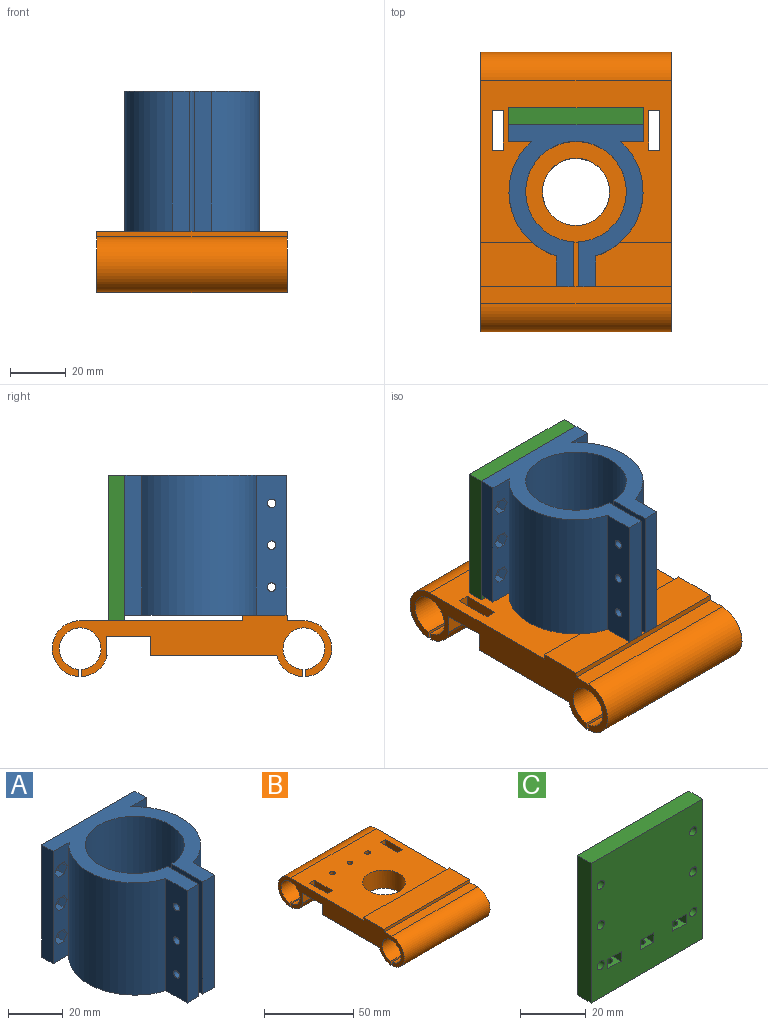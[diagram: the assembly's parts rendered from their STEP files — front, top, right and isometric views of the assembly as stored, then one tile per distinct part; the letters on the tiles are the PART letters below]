
ASSEMBLY  parts=3 mates=2
PART A: 91 faces, bbox 48x58x50 mm
  f0: cylinder r=24mm len=50mm, axis (0,0,-1), area 2547.5mm2, adj f1,f13,f14,f15
  f1: plane 50x8.13mm, normal (0,-1,0), area 331.4mm2, adj f0,f2,f14,f15,f43,f44,f45,f46
  f2: plane 50x6mm, normal (1,0,0), area 300mm2, adj f1,f3,f14,f15
  f3: plane 50x48mm, normal (0,1,0), area 2354.7mm2, adj f2,f4,f14,f15,f64,f65,f66,f88
  f4: plane 50x6mm, normal (-1,0,0), area 300mm2, adj f3,f5,f14,f15
  f5: plane 50x8.13mm, normal (0,-1,0), area 331.4mm2, adj f4,f6,f14,f15,f67,f68,f69,f70
  f6: cylinder r=24mm len=50mm, axis (0,0,-1), area 2547.5mm2, adj f5,f7,f14,f15
  f7: plane 50x11.02mm, normal (-1,0,0), area 528.5mm2, adj f6,f8,f14,f15,f40,f41,f42
  f8: plane 50x6mm, normal (0,-1,0), area 300mm2, adj f7,f9,f14,f15
  f9: plane 50x16.01mm, normal (1,0,0), area 777.7mm2, adj f8,f10,f14,f15,f40,f41,f42
  f10: cylinder r=18mm len=50mm, axis (0,0,-1), area 5554.8mm2, adj f9,f11,f14,f15
  f11: plane 50x16.01mm, normal (-1,0,0), area 777.7mm2, adj f10,f12,f14,f15,f37,f38,f39
  f12: plane 50x6mm, normal (0,-1,0), area 300mm2, adj f11,f13,f14,f15
  f13: plane 50x11.02mm, normal (1,0,0), area 476.2mm2, adj f0,f12,f14,f15,f16,f17,f18,f19
  f14: plane 57.98x48mm, normal (0,0,1), area 1061.7mm2, adj f0,f1,f2,f3,f4,f5,f6,f7
  f15: plane 57.98x48mm, normal (0,0,-1), area 1061.7mm2, adj f0,f1,f2,f3,f4,f5,f6,f7
  f16: plane 3.3x3.1mm, normal (0,0,1), area 10.2mm2, adj f13,f17,f21,f22
  f17: plane 3.3x2.68mm, normal (0,-0.87,0.5), area 10.2mm2, adj f13,f16,f18,f22
  f18: plane 3.3x2.68mm, normal (0,-0.87,-0.5), area 10.2mm2, adj f13,f17,f19,f22
  f19: plane 3.3x3.1mm, normal (0,0,-1), area 10.2mm2, adj f13,f18,f20,f22
  f20: plane 3.3x2.68mm, normal (0,0.87,-0.5), area 10.2mm2, adj f13,f19,f21,f22
  f21: plane 3.3x2.68mm, normal (0,0.87,0.5), area 10.2mm2, adj f13,f16,f20,f22
  f22: plane 6.2x5.37mm, normal (1,0,0), area 17.4mm2, adj f16,f17,f18,f19,f20,f21,f39
  f23: plane 3.3x3.1mm, normal (0,0,1), area 10.2mm2, adj f13,f24,f28,f29
  f24: plane 3.3x2.68mm, normal (0,-0.87,0.5), area 10.2mm2, adj f13,f23,f25,f29
  f25: plane 3.3x2.68mm, normal (0,-0.87,-0.5), area 10.2mm2, adj f13,f24,f26,f29
  f26: plane 3.3x3.1mm, normal (0,0,-1), area 10.2mm2, adj f13,f25,f27,f29
  f27: plane 3.3x2.68mm, normal (0,0.87,-0.5), area 10.2mm2, adj f13,f26,f28,f29
  f28: plane 3.3x2.68mm, normal (0,0.87,0.5), area 10.2mm2, adj f13,f23,f27,f29
  f29: plane 6.2x5.37mm, normal (1,0,0), area 17.4mm2, adj f23,f24,f25,f26,f27,f28,f38
  f30: plane 3.3x3.1mm, normal (0,0,1), area 10.2mm2, adj f13,f31,f35,f36
  f31: plane 3.3x2.68mm, normal (0,-0.87,0.5), area 10.2mm2, adj f13,f30,f32,f36
  f32: plane 3.3x2.68mm, normal (0,-0.87,-0.5), area 10.2mm2, adj f13,f31,f33,f36
  f33: plane 3.3x3.1mm, normal (0,0,-1), area 10.2mm2, adj f13,f32,f34,f36
  f34: plane 3.3x2.68mm, normal (0,0.87,-0.5), area 10.2mm2, adj f13,f33,f35,f36
  f35: plane 3.3x2.68mm, normal (0,0.87,0.5), area 10.2mm2, adj f13,f30,f34,f36
  f36: plane 6.2x5.37mm, normal (1,0,0), area 17.4mm2, adj f30,f31,f32,f33,f34,f35,f37
  f37: cylinder r=1.55mm len=3.1mm, axis (1,0,0), area 26.3mm2, adj f11,f36
  f38: cylinder r=1.55mm len=3.1mm, axis (1,0,0), area 26.3mm2, adj f11,f29
  f39: cylinder r=1.55mm len=3.1mm, axis (1,0,0), area 26.3mm2, adj f11,f22
  f40: cylinder r=1.55mm len=6mm, axis (1,0,0), area 58.4mm2, adj f7,f9
  f41: cylinder r=1.55mm len=6mm, axis (1,0,0), area 58.4mm2, adj f7,f9
  f42: cylinder r=1.55mm len=6mm, axis (1,0,0), area 58.4mm2, adj f7,f9
  f43: plane 3.3x3.1mm, normal (0,0,1), area 10.2mm2, adj f1,f44,f48,f49
  f44: plane 3.3x2.68mm, normal (-0.87,0,0.5), area 10.2mm2, adj f1,f43,f45,f49
  f45: plane 3.3x2.68mm, normal (-0.87,0,-0.5), area 10.2mm2, adj f1,f44,f46,f49
  f46: plane 3.3x3.1mm, normal (0,0,-1), area 10.2mm2, adj f1,f45,f47,f49
  f47: plane 3.3x2.68mm, normal (0.87,0,-0.5), area 10.2mm2, adj f1,f46,f48,f49
  f48: plane 3.3x2.68mm, normal (0.87,0,0.5), area 10.2mm2, adj f1,f43,f47,f49
  f49: plane 6.2x5.37mm, normal (0,-1,0), area 17.4mm2, adj f43,f44,f45,f46,f47,f48,f66
  f50: plane 3.3x3.1mm, normal (0,0,1), area 10.2mm2, adj f1,f51,f55,f56
  f51: plane 3.3x2.68mm, normal (-0.87,0,0.5), area 10.2mm2, adj f1,f50,f52,f56
  f52: plane 3.3x2.68mm, normal (-0.87,0,-0.5), area 10.2mm2, adj f1,f51,f53,f56
  f53: plane 3.3x3.1mm, normal (0,0,-1), area 10.2mm2, adj f1,f52,f54,f56
  f54: plane 3.3x2.68mm, normal (0.87,0,-0.5), area 10.2mm2, adj f1,f53,f55,f56
  f55: plane 3.3x2.68mm, normal (0.87,0,0.5), area 10.2mm2, adj f1,f50,f54,f56
  f56: plane 6.2x5.37mm, normal (0,-1,0), area 17.4mm2, adj f50,f51,f52,f53,f54,f55,f65
  f57: plane 3.3x3.1mm, normal (0,0,1), area 10.2mm2, adj f1,f58,f62,f63
  f58: plane 3.3x2.68mm, normal (-0.87,0,0.5), area 10.2mm2, adj f1,f57,f59,f63
  f59: plane 3.3x2.68mm, normal (-0.87,0,-0.5), area 10.2mm2, adj f1,f58,f60,f63
  f60: plane 3.3x3.1mm, normal (0,0,-1), area 10.2mm2, adj f1,f59,f61,f63
  f61: plane 3.3x2.68mm, normal (0.87,0,-0.5), area 10.2mm2, adj f1,f60,f62,f63
  f62: plane 3.3x2.68mm, normal (0.87,0,0.5), area 10.2mm2, adj f1,f57,f61,f63
  f63: plane 6.2x5.37mm, normal (0,-1,0), area 17.4mm2, adj f57,f58,f59,f60,f61,f62,f64
  f64: cylinder r=1.55mm len=3.1mm, axis (0,-1,0), area 26.3mm2, adj f3,f63
  f65: cylinder r=1.55mm len=3.1mm, axis (0,-1,0), area 26.3mm2, adj f3,f56
  f66: cylinder r=1.55mm len=3.1mm, axis (0,-1,0), area 26.3mm2, adj f3,f49
  f67: plane 3.3x2.68mm, normal (0.87,0,0.5), area 10.2mm2, adj f5,f68,f72,f73
  f68: plane 3.3x3.1mm, normal (0,0,1), area 10.2mm2, adj f5,f67,f69,f73
  f69: plane 3.3x2.68mm, normal (-0.87,0,0.5), area 10.2mm2, adj f5,f68,f70,f73
  f70: plane 3.3x2.68mm, normal (-0.87,0,-0.5), area 10.2mm2, adj f5,f69,f71,f73
  f71: plane 3.3x3.1mm, normal (0,0,-1), area 10.2mm2, adj f5,f70,f72,f73
  f72: plane 3.3x2.68mm, normal (0.87,0,-0.5), area 10.2mm2, adj f5,f67,f71,f73
  f73: plane 6.2x5.37mm, normal (0,-1,0), area 17.4mm2, adj f67,f68,f69,f70,f71,f72,f90
  f74: plane 3.3x2.68mm, normal (0.87,0,0.5), area 10.2mm2, adj f5,f75,f79,f80
  f75: plane 3.3x3.1mm, normal (0,0,1), area 10.2mm2, adj f5,f74,f76,f80
  f76: plane 3.3x2.68mm, normal (-0.87,0,0.5), area 10.2mm2, adj f5,f75,f77,f80
  f77: plane 3.3x2.68mm, normal (-0.87,0,-0.5), area 10.2mm2, adj f5,f76,f78,f80
  f78: plane 3.3x3.1mm, normal (0,0,-1), area 10.2mm2, adj f5,f77,f79,f80
  f79: plane 3.3x2.68mm, normal (0.87,0,-0.5), area 10.2mm2, adj f5,f74,f78,f80
  f80: plane 6.2x5.37mm, normal (0,-1,0), area 17.4mm2, adj f74,f75,f76,f77,f78,f79,f89
  f81: plane 3.3x2.68mm, normal (0.87,0,0.5), area 10.2mm2, adj f5,f82,f86,f87
  f82: plane 3.3x3.1mm, normal (0,0,1), area 10.2mm2, adj f5,f81,f83,f87
  f83: plane 3.3x2.68mm, normal (-0.87,0,0.5), area 10.2mm2, adj f5,f82,f84,f87
  f84: plane 3.3x2.68mm, normal (-0.87,0,-0.5), area 10.2mm2, adj f5,f83,f85,f87
  f85: plane 3.3x3.1mm, normal (0,0,-1), area 10.2mm2, adj f5,f84,f86,f87
  f86: plane 3.3x2.68mm, normal (0.87,0,-0.5), area 10.2mm2, adj f5,f81,f85,f87
  f87: plane 6.2x5.37mm, normal (0,-1,0), area 17.4mm2, adj f81,f82,f83,f84,f85,f86,f88
  f88: cylinder r=1.55mm len=3.1mm, axis (0,-1,0), area 26.3mm2, adj f3,f87
  f89: cylinder r=1.55mm len=3.1mm, axis (0,-1,0), area 26.3mm2, adj f3,f80
  f90: cylinder r=1.55mm len=3.1mm, axis (0,-1,0), area 26.3mm2, adj f3,f73
PART B: 32 faces, bbox 68x100x22 mm
  f0: plane 5.58x4mm, normal (0,-1,0), area 22.3mm2, adj f4,f17,f19,f20
  f1: plane 5.58x4mm, normal (0,-1,0), area 22.3mm2, adj f4,f17,f21,f22
  f2: plane 100x21.99mm, normal (1,0,0), area 996.1mm2, adj f3,f4,f5,f7,f8,f9,f10,f11
  f3: plane 68x6mm, normal (0,0,1), area 408mm2, adj f2,f6,f16,f24
  f4: plane 68x58mm, normal (0,0,1), area 3357mm2, adj f0,f1,f2,f6,f15,f18,f19,f20
  f5: plane 68x45.34mm, normal (0,0,-1), area 2630.6mm2, adj f2,f6,f10,f18,f23
  f6: plane 100x21.99mm, normal (-1,0,0), area 996.1mm2, adj f3,f4,f5,f7,f8,f9,f10,f11
  f7: plane 68x2.55mm, normal (0,1,0), area 173.7mm2, adj f2,f6,f8,f16
  f8: cylinder r=7.45mm len=68mm, axis (-1,0,0), area 3115mm2, adj f2,f6,f7,f9
  f9: plane 68x2.55mm, normal (0,-1,0), area 173.7mm2, adj f2,f6,f8,f10
  f10: cylinder r=10mm len=68mm, axis (-1,0,0), area 856.9mm2, adj f2,f5,f6,f9
  f11: cylinder r=10mm len=68mm, axis (-1,0,0), area 856.9mm2, adj f2,f6,f12,f30
  f12: plane 68x2.55mm, normal (0,1,0), area 173.7mm2, adj f2,f6,f11,f13
  f13: cylinder r=7.45mm len=68mm, axis (-1,0,0), area 3115mm2, adj f2,f6,f12,f14
  f14: plane 68x2.55mm, normal (0,-1,0), area 173.7mm2, adj f2,f6,f13,f15
  f15: cylinder r=10mm len=68mm, axis (-1,0,0), area 2102.3mm2, adj f2,f4,f6,f14
  f16: cylinder r=10mm len=68mm, axis (-1,0,0), area 2102.3mm2, adj f2,f3,f6,f7
  f17: plane 68x15.5mm, normal (0,0,-1), area 919.4mm2, adj f0,f1,f2,f6,f18,f19,f20,f21
  f18: plane 68x12.58mm, normal (0,1,0), area 520.6mm2, adj f2,f4,f5,f6,f17,f19,f20,f21
  f19: plane 14x5.58mm, normal (-1,0,0), area 78.1mm2, adj f0,f4,f17,f18
  f20: plane 14x5.58mm, normal (1,0,0), area 78.1mm2, adj f0,f4,f17,f18
  f21: plane 14x5.58mm, normal (1,0,0), area 78.1mm2, adj f1,f4,f17,f18
  f22: plane 14x5.58mm, normal (-1,0,0), area 78.1mm2, adj f1,f4,f17,f18
  f23: cylinder r=12mm len=24mm, axis (0,0,1), area 948.2mm2, adj f4,f5
  f24: plane 68x2mm, normal (0,-1,0), area 136mm2, adj f2,f3,f6,f26
  f25: plane 68x2mm, normal (0,1,0), area 136mm2, adj f2,f4,f6,f26
  f26: plane 68x16mm, normal (0,0,1), area 1088mm2, adj f2,f6,f24,f25
  f27: cylinder r=1.55mm len=5.58mm, axis (0,0,1), area 54.3mm2, adj f4,f17
  f28: cylinder r=1.55mm len=5.58mm, axis (0,0,1), area 54.3mm2, adj f4,f17
  f29: cylinder r=1.55mm len=5.58mm, axis (0,0,1), area 54.3mm2, adj f4,f17
  f30: plane 68x0.16mm, normal (0,0,1), area 11mm2, adj f2,f6,f11,f31
  f31: plane 68x7mm, normal (0,-1,0), area 476mm2, adj f2,f6,f17,f30
PART C: 27 faces, bbox 48x6x52 mm
  f0: plane 52x48mm, normal (0,1,0), area 2390.9mm2, adj f2,f3,f4,f5,f6,f7,f8,f9
  f1: plane 52x48mm, normal (0,-1,0), area 2390.9mm2, adj f2,f3,f4,f5,f6,f7,f8,f9
  f2: plane 52x6mm, normal (1,0,0), area 312mm2, adj f0,f1,f4,f5
  f3: plane 52x6mm, normal (-1,0,0), area 312mm2, adj f0,f1,f4,f5
  f4: plane 48x6mm, normal (0,0,1), area 288mm2, adj f0,f1,f2,f3
  f5: plane 48x6mm, normal (0,0,-1), area 265.4mm2, adj f0,f1,f2,f3,f24,f25,f26
  f6: cylinder r=1.55mm len=6mm, axis (0,1,0), area 58.4mm2, adj f0,f1
  f7: cylinder r=1.55mm len=6mm, axis (0,1,0), area 58.4mm2, adj f0,f1
  f8: cylinder r=1.55mm len=6mm, axis (0,1,0), area 58.4mm2, adj f0,f1
  f9: cylinder r=1.55mm len=6mm, axis (0,1,0), area 58.4mm2, adj f0,f1
  f10: cylinder r=1.55mm len=6mm, axis (0,1,0), area 58.4mm2, adj f0,f1
  f11: cylinder r=1.55mm len=6mm, axis (0,1,0), area 58.4mm2, adj f0,f1
  f12: plane 6x5.7mm, normal (0,0,-1), area 34.2mm2, adj f0,f1,f13,f15
  f13: plane 6x3.5mm, normal (1,0,0), area 21mm2, adj f0,f1,f12,f14
  f14: plane 6x5.7mm, normal (0,0,1), area 26.7mm2, adj f0,f1,f13,f15,f26
  f15: plane 6x3.5mm, normal (-1,0,0), area 21mm2, adj f0,f1,f12,f14
  f16: plane 6x5.7mm, normal (0,0,-1), area 34.2mm2, adj f0,f1,f17,f19
  f17: plane 6x3.5mm, normal (1,0,0), area 21mm2, adj f0,f1,f16,f18
  f18: plane 6x5.7mm, normal (0,0,1), area 26.7mm2, adj f0,f1,f17,f19,f25
  f19: plane 6x3.5mm, normal (-1,0,0), area 21mm2, adj f0,f1,f16,f18
  f20: plane 6x5.7mm, normal (0,0,-1), area 34.2mm2, adj f0,f1,f21,f23
  f21: plane 6x3.5mm, normal (1,0,0), area 21mm2, adj f0,f1,f20,f22
  f22: plane 6x5.7mm, normal (0,0,1), area 26.7mm2, adj f0,f1,f21,f23,f24
  f23: plane 6x3.5mm, normal (-1,0,0), area 21mm2, adj f0,f1,f20,f22
  f24: cylinder r=1.55mm len=9.2mm, axis (0,0,-1), area 89.6mm2, adj f5,f22
  f25: cylinder r=1.55mm len=9.2mm, axis (0,0,-1), area 89.6mm2, adj f5,f18
  f26: cylinder r=1.55mm len=9.2mm, axis (0,0,-1), area 89.6mm2, adj f5,f14
PLACE A t=(40.77,1.26,15.16)mm
PLACE B t=(6.77,1.26,3.16)mm
PLACE C t=(6.77,1.26,13.16)mm
MATE fastened A.f3 <-> C.f1  axis (0,1,0) through (16.77,25.26,65.16)mm
MATE fastened A.f10 <-> B.f23  axis (0,0,-1) through (40.77,1.26,15.16)mm
